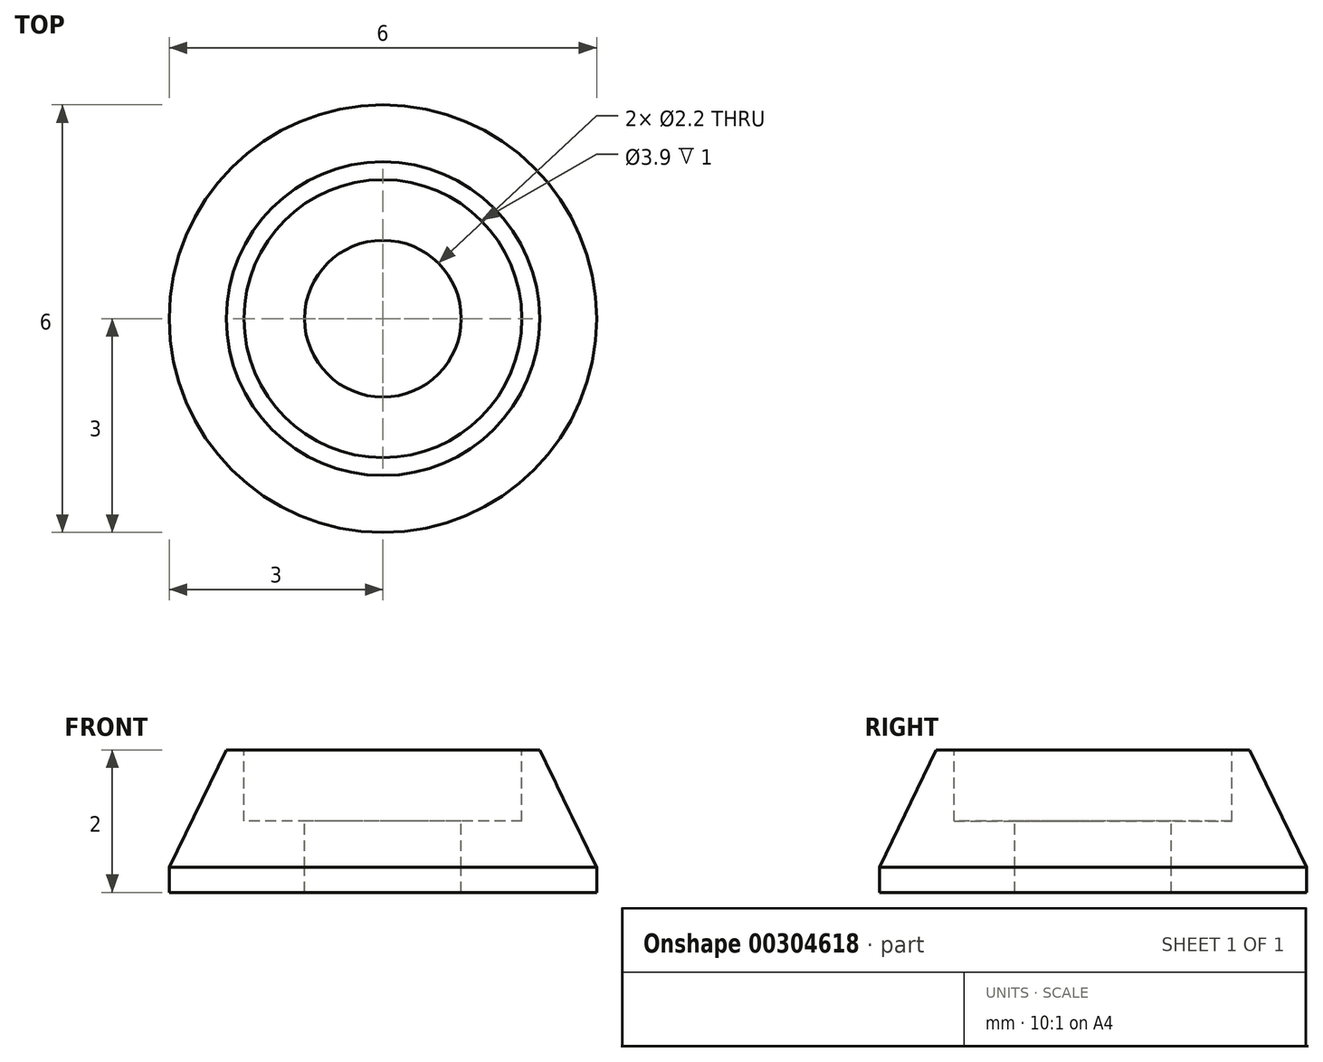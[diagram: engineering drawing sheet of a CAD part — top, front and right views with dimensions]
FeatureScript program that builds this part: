
annotation { "Feature Type Name" : "Feature", "Feature Type Description" : "" }
export const myFeature = defineFeature(function(context is Context, id is Id, definition is map)
    precondition{}
    {
        {
            assignVariable(context, id + "F0", {"name" : "LipHeight", "anyValue" : 0.35 * mm});
        }
        {
            assignVariable(context, id + "F1", {"name" : "WasherHeight", "anyValue" : 1 * mm});
        }
        {
            assignVariable(context, id + "F2", {"name" : "PlateauHeight", "anyValue" : 1 * mm});
        }
        {
            var Q0;
            Q0=qCreatedBy(makeId("Top.planeOp"),FACE);
            cPlane(context, id + "F3", {"entities" : qUnion([Q0]), "cplaneType" : CPlaneType.OFFSET, "offset" : 0 * mm, "width" : 150 * mm, "height" : 150 * mm});
        }
        {
            var Q0;
            Q0=qCreatedBy(id+"F3.planeOp",FACE);
            cPlane(context, id + "F4", {"entities" : qUnion([Q0]), "cplaneType" : CPlaneType.OFFSET, "offset" : getVariable(context, 'LipHeight'), "width" : 150 * mm, "height" : 150 * mm});
        }
        {
            var Q0;
            Q0=qCreatedBy(id+"F3.planeOp",FACE);
            cPlane(context, id + "F5", {"entities" : qUnion([Q0]), "cplaneType" : CPlaneType.OFFSET, "offset" : getVariable(context, 'WasherHeight'), "width" : 150 * mm, "height" : 150 * mm});
        }
        {
            var Q0;
            Q0=qCreatedBy(id+"F5.planeOp",FACE);
            cPlane(context, id + "F6", {"entities" : qUnion([Q0]), "cplaneType" : CPlaneType.OFFSET, "offset" : getVariable(context, 'PlateauHeight'), "width" : 150 * mm, "height" : 150 * mm});
        }
        {
            var Q0;
            Q0=qCreatedBy(makeId("Top.planeOp"),FACE);
            var sketch = newSketch(context, id + "F7", { "sketchPlane" : qUnion([Q0])});
            skCircle(sketch, "E0", {"center": v(0, 0) * mm, "radius": 3 * mm});
            skSolve(sketch);
        }
        {
            var Q0;
            Q0=qCreatedBy(id+"F4.planeOp",FACE);
            var sketch = newSketch(context, id + "F8", { "sketchPlane" : qUnion([Q0])});
            skCircle(sketch, "E1.0", {"center": v(0, 0) * mm, "radius": 3 * mm});
            skSolve(sketch);
        }
        {
            var Q0;
            Q0=qCreatedBy(id+"F6.planeOp",FACE);
            var sketch = newSketch(context, id + "F9", { "sketchPlane" : qUnion([Q0])});
            skCircle(sketch, "E2", {"center": v(0, 0) * mm, "radius": 1.95 * mm});
            skSolve(sketch);
        }
        {
            var Q0;
            Q0=qCreatedBy(id+"F6.planeOp",FACE);
            var sketch = newSketch(context, id + "F10", { "sketchPlane" : qUnion([Q0])});
            skCircle(sketch, "E3", {"center": v(0, 0) * mm, "radius": 2.2 * mm});
            skSolve(sketch);
        }
        {
            var Q0;
            Q0=qCreatedBy(id+"F5.planeOp",FACE);
            var sketch = newSketch(context, id + "F11", { "sketchPlane" : qUnion([Q0])});
            skCircle(sketch, "E4.0", {"center": v(0, 0) * mm, "radius": 1.95 * mm});
            skSolve(sketch);
        }
        {
            var Q0;
            Q0=qCreatedBy(makeId("Top.planeOp"),FACE);
            var sketch = newSketch(context, id + "F12", { "sketchPlane" : qUnion([Q0])});
            skCircle(sketch, "E5", {"center": v(0, 0) * mm, "radius": 1.1 * mm});
            skSolve(sketch);
        }
        {
            var Q0;
            Q0=qCreatedBy(id+"F5.planeOp",FACE);
            var sketch = newSketch(context, id + "F13", { "sketchPlane" : qUnion([Q0])});
            skCircle(sketch, "E6.0.0", {"center": v(0, 0) * mm, "radius": 1.1 * mm});
            skSolve(sketch);
        }
        {
            var Q0;
            Q0=makeQuery(id+"F7.imprint","IMPRINT",FACE,{"disambiguationData":[TD([[makeQuery(id+"F7.imprint","IMPRINT",EDGE,{"derivedFrom":sQuery(id+"F7.wireOp",EDGE,"E0")}),1.0]])]});
            var Q1;
            Q1=makeQuery(id+"F8.imprint","IMPRINT",FACE,{"disambiguationData":[TD([[makeQuery(id+"F8.imprint","IMPRINT",EDGE,{"derivedFrom":sQuery(id+"F8.wireOp",EDGE,"E1.0")}),1.0]])]});
            loft(context, id + "F14", {"sheetProfilesArray" : [{ "sheetProfileEntities" : qUnion([Q0]) }, { "sheetProfileEntities" : qUnion([Q1]) }]});
        }
        {
            var Q0;
            Q0 = qSketchRegion(id + "F10", true);
            var Q1;
            Q1 = qSketchRegion(id + "F8", true);
            loft(context, id + "F15", {"sheetProfilesArray" : [{ "sheetProfileEntities" : qUnion([Q0]) }, { "sheetProfileEntities" : qUnion([Q1]) }]});
        }
        {
            var Q1;
            Q1 = qSketchRegion(id + "F9", true);
            var Q2;
            Q2 = qSketchRegion(id + "F11", true);
            loft(context, id + "F16", {"operationType" : NewBodyOperationType.REMOVE, "sheetProfilesArray" : [{ "sheetProfileEntities" : qUnion([Q1]) }, { "sheetProfileEntities" : qUnion([Q2]) }]});
        }
        {
            var Q1;
            Q1=makeQuery(id+"F13.imprint","IMPRINT",FACE,{"disambiguationData":[TD([[makeQuery(id+"F13.imprint","IMPRINT",EDGE,{"derivedFrom":sQuery(id+"F13.wireOp",EDGE,"E6.0.0")}),1.0]])]});
            var Q2;
            Q2=makeQuery(id+"F12.imprint","IMPRINT",FACE,{"disambiguationData":[TD([[makeQuery(id+"F12.imprint","IMPRINT",EDGE,{"derivedFrom":sQuery(id+"F12.wireOp",EDGE,"E5")}),1.0]])]});
            loft(context, id + "F17", {"operationType" : NewBodyOperationType.REMOVE, "sheetProfilesArray" : [{ "sheetProfileEntities" : qUnion([Q1]) }, { "sheetProfileEntities" : qUnion([Q2]) }]});
        }
    });
